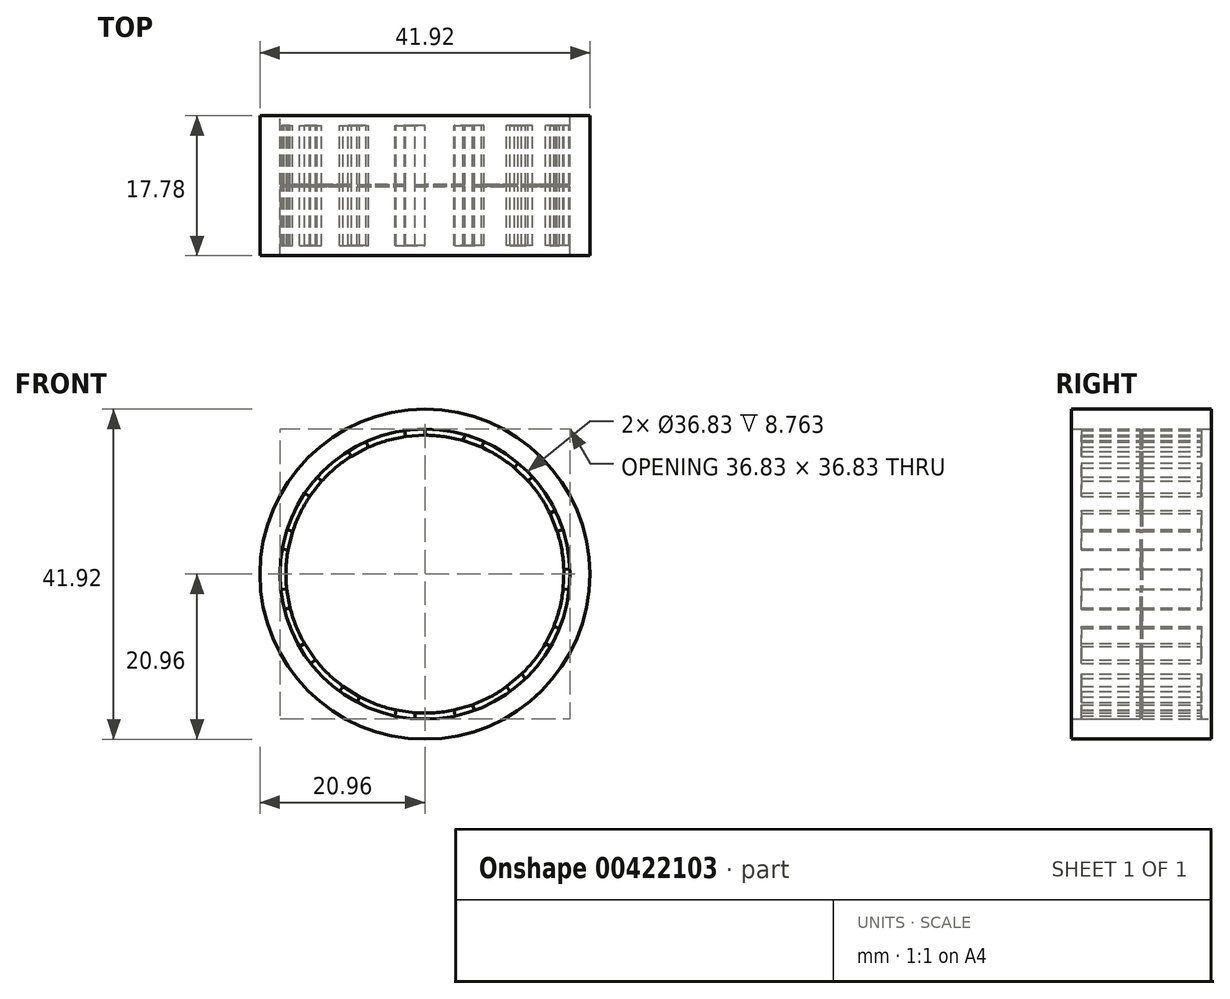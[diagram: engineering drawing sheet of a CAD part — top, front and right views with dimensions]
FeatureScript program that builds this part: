
annotation { "Feature Type Name" : "Feature", "Feature Type Description" : "" }
export const myFeature = defineFeature(function(context is Context, id is Id, definition is map)
    precondition{}
    {
        {
            var Q0;
            Q0=qCreatedBy(makeId("Front.planeOp"),FACE);
            var sketch = newSketch(context, id + "F0", { "sketchPlane" : qUnion([Q0])});
            skCircle(sketch, "E0", {"center": v(0, 0) * mm, "radius": 20.96 * mm});
            skCircle(sketch, "E1", {"center": v(0, 0) * mm, "radius": 18.41 * mm});
            skSolve(sketch);
        }
        {
            var Q0;
            Q0=makeQuery(id+"F0.imprint","IMPRINT",FACE,{"disambiguationData":[TD([[makeQuery(id+"F0.imprint","IMPRINT",EDGE,{"derivedFrom":sQuery(id+"F0.wireOp",EDGE,"E1")}),1.0]])]});
            var sketch = newSketch(context, id + "F1", { "sketchPlane" : qUnion([Q0])});
            skLineSegment(sketch, "E2", {"start": v(0, 18.41) * mm, "end": v(0, 17.65) * mm});
            skLineSegment(sketch, "E3", {"start": v(-2.56, 18.24) * mm, "end": v(-2.46, 17.48) * mm});
            skLineSegment(sketch, "E4", {"start": v(-2.46, 17.48) * mm, "end": v(0, 17.65) * mm});
            skArc(sketch, "E5", {"start": v(0, 18.41) * mm, "mid": v(-1.3, 18.5) * mm, "end": v(-2.56, 18.24) * mm});
            skLineSegment(sketch, "E6.1.0", {"start": v(-7.5, 16.82) * mm, "end": v(-7.18, 16.13) * mm});
            skArc(sketch, "E6.1.1", {"start": v(-7.5, 16.82) * mm, "mid": v(-8.7, 16.37) * mm, "end": v(-9.76, 15.62) * mm});
            skLineSegment(sketch, "E6.1.2", {"start": v(-9.35, 14.97) * mm, "end": v(-7.18, 16.13) * mm});
            skLineSegment(sketch, "E6.1.3", {"start": v(-9.76, 15.62) * mm, "end": v(-9.35, 14.97) * mm});
            skLineSegment(sketch, "E6.2.0", {"start": v(-13.69, 12.32) * mm, "end": v(-13.12, 11.81) * mm});
            skArc(sketch, "E6.2.1", {"start": v(-13.69, 12.32) * mm, "mid": v(-14.6, 11.41) * mm, "end": v(-15.27, 10.3) * mm});
            skLineSegment(sketch, "E6.2.2", {"start": v(-14.64, 9.87) * mm, "end": v(-13.12, 11.81) * mm});
            skLineSegment(sketch, "E6.2.3", {"start": v(-15.27, 10.3) * mm, "end": v(-14.64, 9.87) * mm});
            skLineSegment(sketch, "E6.3.0", {"start": v(-17.51, 5.7) * mm, "end": v(-16.79, 5.46) * mm});
            skArc(sketch, "E6.3.1", {"start": v(-17.51, 5.7) * mm, "mid": v(-17.99, 4.49) * mm, "end": v(-18.14, 3.2) * mm});
            skLineSegment(sketch, "E6.3.2", {"start": v(-17.38, 3.07) * mm, "end": v(-16.79, 5.46) * mm});
            skLineSegment(sketch, "E6.3.3", {"start": v(-18.14, 3.2) * mm, "end": v(-17.38, 3.07) * mm});
            skLineSegment(sketch, "E6.4.0", {"start": v(-18.31, -1.92) * mm, "end": v(-17.56, -1.85) * mm});
            skArc(sketch, "E6.4.1", {"start": v(-18.31, -1.92) * mm, "mid": v(-18.26, -3.22) * mm, "end": v(-17.87, -4.45) * mm});
            skLineSegment(sketch, "E6.4.2", {"start": v(-17.13, -4.27) * mm, "end": v(-17.56, -1.85) * mm});
            skLineSegment(sketch, "E6.4.3", {"start": v(-17.87, -4.45) * mm, "end": v(-17.13, -4.27) * mm});
            skLineSegment(sketch, "E6.5.0", {"start": v(-15.95, -9.2) * mm, "end": v(-15.29, -8.83) * mm});
            skArc(sketch, "E6.5.1", {"start": v(-15.95, -9.2) * mm, "mid": v(-15.37, -10.37) * mm, "end": v(-14.51, -11.34) * mm});
            skLineSegment(sketch, "E6.5.2", {"start": v(-13.91, -10.87) * mm, "end": v(-15.29, -8.83) * mm});
            skLineSegment(sketch, "E6.5.3", {"start": v(-14.51, -11.34) * mm, "end": v(-13.91, -10.87) * mm});
            skLineSegment(sketch, "E6.6.0", {"start": v(-10.82, -14.9) * mm, "end": v(-10.38, -14.28) * mm});
            skArc(sketch, "E6.6.1", {"start": v(-10.82, -14.9) * mm, "mid": v(-9.82, -15.72) * mm, "end": v(-8.65, -16.26) * mm});
            skLineSegment(sketch, "E6.6.2", {"start": v(-8.29, -15.59) * mm, "end": v(-10.38, -14.28) * mm});
            skLineSegment(sketch, "E6.6.3", {"start": v(-8.65, -16.26) * mm, "end": v(-8.29, -15.59) * mm});
            skLineSegment(sketch, "E6.7.0", {"start": v(-3.83, -18.01) * mm, "end": v(-3.67, -17.27) * mm});
            skArc(sketch, "E6.7.1", {"start": v(-3.83, -18.01) * mm, "mid": v(-2.58, -18.36) * mm, "end": v(-1.28, -18.37) * mm});
            skLineSegment(sketch, "E6.7.2", {"start": v(-1.23, -17.6) * mm, "end": v(-3.67, -17.27) * mm});
            skLineSegment(sketch, "E6.7.3", {"start": v(-1.28, -18.37) * mm, "end": v(-1.23, -17.6) * mm});
            skLineSegment(sketch, "E6.8.0", {"start": v(3.83, -18.01) * mm, "end": v(3.67, -17.27) * mm});
            skArc(sketch, "E6.8.1", {"start": v(3.83, -18.01) * mm, "mid": v(5.11, -17.82) * mm, "end": v(6.3, -17.3) * mm});
            skLineSegment(sketch, "E6.8.2", {"start": v(6.04, -16.59) * mm, "end": v(3.67, -17.27) * mm});
            skLineSegment(sketch, "E6.8.3", {"start": v(6.3, -17.3) * mm, "end": v(6.04, -16.59) * mm});
            skLineSegment(sketch, "E6.9.0", {"start": v(10.82, -14.9) * mm, "end": v(10.38, -14.28) * mm});
            skArc(sketch, "E6.9.1", {"start": v(10.82, -14.9) * mm, "mid": v(11.92, -14.2) * mm, "end": v(12.8, -13.25) * mm});
            skLineSegment(sketch, "E6.9.2", {"start": v(12.26, -12.7) * mm, "end": v(10.38, -14.28) * mm});
            skLineSegment(sketch, "E6.9.3", {"start": v(12.8, -13.25) * mm, "end": v(12.26, -12.7) * mm});
            skLineSegment(sketch, "E6.10.0", {"start": v(15.95, -9.2) * mm, "end": v(15.29, -8.83) * mm});
            skArc(sketch, "E6.10.1", {"start": v(15.95, -9.2) * mm, "mid": v(16.66, -8.13) * mm, "end": v(17.07, -6.9) * mm});
            skLineSegment(sketch, "E6.10.2", {"start": v(16.37, -6.61) * mm, "end": v(15.29, -8.83) * mm});
            skLineSegment(sketch, "E6.10.3", {"start": v(17.07, -6.9) * mm, "end": v(16.37, -6.61) * mm});
            skLineSegment(sketch, "E6.11.0", {"start": v(18.31, -1.92) * mm, "end": v(17.56, -1.85) * mm});
            skArc(sketch, "E6.11.1", {"start": v(18.31, -1.92) * mm, "mid": v(18.53, -0.65) * mm, "end": v(18.4, 0.64) * mm});
            skLineSegment(sketch, "E6.11.2", {"start": v(17.64, 0.62) * mm, "end": v(17.56, -1.85) * mm});
            skLineSegment(sketch, "E6.11.3", {"start": v(18.4, 0.64) * mm, "end": v(17.64, 0.62) * mm});
            skLineSegment(sketch, "E6.12.0", {"start": v(17.51, 5.7) * mm, "end": v(16.79, 5.46) * mm});
            skArc(sketch, "E6.12.1", {"start": v(17.51, 5.7) * mm, "mid": v(17.2, 6.95) * mm, "end": v(16.55, 8.07) * mm});
            skLineSegment(sketch, "E6.12.2", {"start": v(15.87, 7.74) * mm, "end": v(16.79, 5.46) * mm});
            skLineSegment(sketch, "E6.12.3", {"start": v(16.55, 8.07) * mm, "end": v(15.87, 7.74) * mm});
            skLineSegment(sketch, "E6.13.0", {"start": v(13.69, 12.32) * mm, "end": v(13.12, 11.81) * mm});
            skArc(sketch, "E6.13.1", {"start": v(13.69, 12.32) * mm, "mid": v(12.88, 13.34) * mm, "end": v(11.84, 14.1) * mm});
            skLineSegment(sketch, "E6.13.2", {"start": v(11.35, 13.52) * mm, "end": v(13.12, 11.81) * mm});
            skLineSegment(sketch, "E6.13.3", {"start": v(11.84, 14.1) * mm, "end": v(11.35, 13.52) * mm});
            skLineSegment(sketch, "E6.14.0", {"start": v(7.5, 16.82) * mm, "end": v(7.18, 16.13) * mm});
            skArc(sketch, "E6.14.1", {"start": v(7.5, 16.82) * mm, "mid": v(6.34, 17.42) * mm, "end": v(5.08, 17.7) * mm});
            skLineSegment(sketch, "E6.14.2", {"start": v(4.87, 16.97) * mm, "end": v(7.18, 16.13) * mm});
            skLineSegment(sketch, "E6.14.3", {"start": v(5.08, 17.7) * mm, "end": v(4.87, 16.97) * mm});
            skPoint(sketch, "E6.center", {"position": v(0, 0) * mm});
            skSolve(sketch);
        }
        {
            var Q0;
            {var subQ1=sQuery(id+"F1.wireOp",EDGE,"E2");Q0=makeQuery(id+"F1.imprint","IMPRINT",FACE,{"disambiguationData":[TD([[makeQuery(id+"F1.imprint","IMPRINT",EDGE,{"derivedFrom":subQ1}),1.0]])]});}
            var sketch = newSketch(context, id + "F2", { "sketchPlane" : qUnion([Q0])});
            skCircle(sketch, "E7", {"center": v(0, 0) * mm, "radius": 17.65 * mm});
            skSolve(sketch);
        }
        {
            var Q0;
            Q0 = qSketchRegion(id + "F0", true);
            extrude(context, id + "F3", {"entities" : qUnion([Q0]), "endBound" : BoundingType.SYMMETRIC, "depth" : 17.78 * mm});
        }
        {
            var Q0;
            Q0 = qSketchRegion(id + "F1", true);
            extrude(context, id + "F4", {"entities" : qUnion([Q0]), "operationType" : NewBodyOperationType.ADD, "endBound" : BoundingType.SYMMETRIC, "depth" : 15.24 * mm});
        }
        {
            var Q0;
            {var subQ1=makeQuery(id+"F1.imprint","IMPRINT",EDGE,{"derivedFrom":sQuery(id+"F1.wireOp",EDGE,"E6.12.2")});Q0=makeQuery(id+"F2.imprint","IMPRINT",FACE,{"disambiguationData":[TD([[makeQuery(id+"F2.imprint","IMPRINT",EDGE,{"derivedFrom":subQ1}),1.0]])]});}
            var Q1;
            {var subQ1=makeQuery(id+"F1.imprint","IMPRINT",EDGE,{"derivedFrom":sQuery(id+"F1.wireOp",EDGE,"E6.13.2")});Q1=makeQuery(id+"F2.imprint","IMPRINT",FACE,{"disambiguationData":[TD([[makeQuery(id+"F2.imprint","IMPRINT",EDGE,{"derivedFrom":subQ1}),1.0]])]});}
            var Q2;
            {var subQ1=makeQuery(id+"F1.imprint","IMPRINT",EDGE,{"derivedFrom":sQuery(id+"F1.wireOp",EDGE,"E6.14.2")});Q2=makeQuery(id+"F2.imprint","IMPRINT",FACE,{"disambiguationData":[TD([[makeQuery(id+"F2.imprint","IMPRINT",EDGE,{"derivedFrom":subQ1}),1.0]])]});}
            var Q3;
            {var subQ1=makeQuery(id+"F1.imprint","IMPRINT",EDGE,{"derivedFrom":sQuery(id+"F1.wireOp",EDGE,"E4")});Q3=makeQuery(id+"F2.imprint","IMPRINT",FACE,{"disambiguationData":[TD([[makeQuery(id+"F2.imprint","IMPRINT",EDGE,{"derivedFrom":subQ1}),1.0]])]});}
            var Q4;
            {var subQ1=makeQuery(id+"F1.imprint","IMPRINT",EDGE,{"derivedFrom":sQuery(id+"F1.wireOp",EDGE,"E6.1.2")});Q4=makeQuery(id+"F2.imprint","IMPRINT",FACE,{"disambiguationData":[TD([[makeQuery(id+"F2.imprint","IMPRINT",EDGE,{"derivedFrom":subQ1}),1.0]])]});}
            var Q5;
            {var subQ1=makeQuery(id+"F1.imprint","IMPRINT",EDGE,{"derivedFrom":sQuery(id+"F1.wireOp",EDGE,"E6.2.2")});Q5=makeQuery(id+"F2.imprint","IMPRINT",FACE,{"disambiguationData":[TD([[makeQuery(id+"F2.imprint","IMPRINT",EDGE,{"derivedFrom":subQ1}),1.0]])]});}
            var Q6;
            {var subQ1=makeQuery(id+"F1.imprint","IMPRINT",EDGE,{"derivedFrom":sQuery(id+"F1.wireOp",EDGE,"E6.3.2")});Q6=makeQuery(id+"F2.imprint","IMPRINT",FACE,{"disambiguationData":[TD([[makeQuery(id+"F2.imprint","IMPRINT",EDGE,{"derivedFrom":subQ1}),1.0]])]});}
            var Q7;
            {var subQ1=makeQuery(id+"F1.imprint","IMPRINT",EDGE,{"derivedFrom":sQuery(id+"F1.wireOp",EDGE,"E6.4.2")});Q7=makeQuery(id+"F2.imprint","IMPRINT",FACE,{"disambiguationData":[TD([[makeQuery(id+"F2.imprint","IMPRINT",EDGE,{"derivedFrom":subQ1}),1.0]])]});}
            var Q8;
            {var subQ1=makeQuery(id+"F1.imprint","IMPRINT",EDGE,{"derivedFrom":sQuery(id+"F1.wireOp",EDGE,"E6.5.2")});Q8=makeQuery(id+"F2.imprint","IMPRINT",FACE,{"disambiguationData":[TD([[makeQuery(id+"F2.imprint","IMPRINT",EDGE,{"derivedFrom":subQ1}),1.0]])]});}
            var Q9;
            {var subQ1=makeQuery(id+"F1.imprint","IMPRINT",EDGE,{"derivedFrom":sQuery(id+"F1.wireOp",EDGE,"E6.6.2")});Q9=makeQuery(id+"F2.imprint","IMPRINT",FACE,{"disambiguationData":[TD([[makeQuery(id+"F2.imprint","IMPRINT",EDGE,{"derivedFrom":subQ1}),1.0]])]});}
            var Q10;
            {var subQ1=makeQuery(id+"F1.imprint","IMPRINT",EDGE,{"derivedFrom":sQuery(id+"F1.wireOp",EDGE,"E6.7.2")});Q10=makeQuery(id+"F2.imprint","IMPRINT",FACE,{"disambiguationData":[TD([[makeQuery(id+"F2.imprint","IMPRINT",EDGE,{"derivedFrom":subQ1}),1.0]])]});}
            var Q11;
            {var subQ1=makeQuery(id+"F1.imprint","IMPRINT",EDGE,{"derivedFrom":sQuery(id+"F1.wireOp",EDGE,"E6.8.2")});Q11=makeQuery(id+"F2.imprint","IMPRINT",FACE,{"disambiguationData":[TD([[makeQuery(id+"F2.imprint","IMPRINT",EDGE,{"derivedFrom":subQ1}),1.0]])]});}
            var Q12;
            {var subQ1=makeQuery(id+"F1.imprint","IMPRINT",EDGE,{"derivedFrom":sQuery(id+"F1.wireOp",EDGE,"E6.9.2")});Q12=makeQuery(id+"F2.imprint","IMPRINT",FACE,{"disambiguationData":[TD([[makeQuery(id+"F2.imprint","IMPRINT",EDGE,{"derivedFrom":subQ1}),1.0]])]});}
            var Q13;
            {var subQ1=makeQuery(id+"F1.imprint","IMPRINT",EDGE,{"derivedFrom":sQuery(id+"F1.wireOp",EDGE,"E6.10.2")});Q13=makeQuery(id+"F2.imprint","IMPRINT",FACE,{"disambiguationData":[TD([[makeQuery(id+"F2.imprint","IMPRINT",EDGE,{"derivedFrom":subQ1}),1.0]])]});}
            var Q14;
            {var subQ1=makeQuery(id+"F1.imprint","IMPRINT",EDGE,{"derivedFrom":sQuery(id+"F1.wireOp",EDGE,"E6.11.2")});Q14=makeQuery(id+"F2.imprint","IMPRINT",FACE,{"disambiguationData":[TD([[makeQuery(id+"F2.imprint","IMPRINT",EDGE,{"derivedFrom":subQ1}),1.0]])]});}
            var Q15;
            {var subQ1=sQuery(id+"F1.wireOp",EDGE,"E6.2.3");var subQ2=makeQuery(id+"F1.imprint","IMPRINT",EDGE,{"derivedFrom":subQ1});Q15=makeQuery(id+"F2.imprint","IMPRINT",FACE,{"disambiguationData":[TD([[makeQuery(id+"F2.imprint","IMPRINT",EDGE,{"derivedFrom":subQ2}),-1.0]])]});}
            var Q16;
            {var subQ1=sQuery(id+"F1.wireOp",EDGE,"E6.1.3");var subQ2=makeQuery(id+"F1.imprint","IMPRINT",EDGE,{"derivedFrom":subQ1});Q16=makeQuery(id+"F2.imprint","IMPRINT",FACE,{"disambiguationData":[TD([[makeQuery(id+"F2.imprint","IMPRINT",EDGE,{"derivedFrom":subQ2}),-1.0]])]});}
            var Q17;
            {var subQ1=sQuery(id+"F1.wireOp",EDGE,"E3");var subQ2=makeQuery(id+"F1.imprint","IMPRINT",EDGE,{"derivedFrom":subQ1});Q17=makeQuery(id+"F2.imprint","IMPRINT",FACE,{"disambiguationData":[TD([[makeQuery(id+"F2.imprint","IMPRINT",EDGE,{"derivedFrom":subQ2}),-1.0]])]});}
            var Q18;
            {var subQ1=sQuery(id+"F1.wireOp",EDGE,"E2");var subQ2=makeQuery(id+"F1.imprint","IMPRINT",EDGE,{"derivedFrom":subQ1});Q18=makeQuery(id+"F2.imprint","IMPRINT",FACE,{"disambiguationData":[TD([[makeQuery(id+"F2.imprint","IMPRINT",EDGE,{"derivedFrom":subQ2}),1.0]])]});}
            var Q19;
            {var subQ1=sQuery(id+"F1.wireOp",EDGE,"E6.13.3");var subQ2=makeQuery(id+"F1.imprint","IMPRINT",EDGE,{"derivedFrom":subQ1});Q19=makeQuery(id+"F2.imprint","IMPRINT",FACE,{"disambiguationData":[TD([[makeQuery(id+"F2.imprint","IMPRINT",EDGE,{"derivedFrom":subQ2}),-1.0]])]});}
            var Q20;
            {var subQ1=sQuery(id+"F1.wireOp",EDGE,"E6.12.3");var subQ2=makeQuery(id+"F1.imprint","IMPRINT",EDGE,{"derivedFrom":subQ1});Q20=makeQuery(id+"F2.imprint","IMPRINT",FACE,{"disambiguationData":[TD([[makeQuery(id+"F2.imprint","IMPRINT",EDGE,{"derivedFrom":subQ2}),-1.0]])]});}
            var Q21;
            {var subQ1=sQuery(id+"F1.wireOp",EDGE,"E6.3.3");var subQ2=makeQuery(id+"F1.imprint","IMPRINT",EDGE,{"derivedFrom":subQ1});Q21=makeQuery(id+"F2.imprint","IMPRINT",FACE,{"disambiguationData":[TD([[makeQuery(id+"F2.imprint","IMPRINT",EDGE,{"derivedFrom":subQ2}),-1.0]])]});}
            var Q22;
            {var subQ1=sQuery(id+"F1.wireOp",EDGE,"E6.4.3");var subQ2=makeQuery(id+"F1.imprint","IMPRINT",EDGE,{"derivedFrom":subQ1});Q22=makeQuery(id+"F2.imprint","IMPRINT",FACE,{"disambiguationData":[TD([[makeQuery(id+"F2.imprint","IMPRINT",EDGE,{"derivedFrom":subQ2}),-1.0]])]});}
            var Q23;
            {var subQ1=sQuery(id+"F1.wireOp",EDGE,"E6.5.3");var subQ2=makeQuery(id+"F1.imprint","IMPRINT",EDGE,{"derivedFrom":subQ1});Q23=makeQuery(id+"F2.imprint","IMPRINT",FACE,{"disambiguationData":[TD([[makeQuery(id+"F2.imprint","IMPRINT",EDGE,{"derivedFrom":subQ2}),-1.0]])]});}
            var Q24;
            {var subQ1=sQuery(id+"F1.wireOp",EDGE,"E6.7.3");var subQ2=makeQuery(id+"F1.imprint","IMPRINT",EDGE,{"derivedFrom":subQ1});Q24=makeQuery(id+"F2.imprint","IMPRINT",FACE,{"disambiguationData":[TD([[makeQuery(id+"F2.imprint","IMPRINT",EDGE,{"derivedFrom":subQ2}),-1.0]])]});}
            var Q25;
            {var subQ1=sQuery(id+"F1.wireOp",EDGE,"E6.6.3");var subQ2=makeQuery(id+"F1.imprint","IMPRINT",EDGE,{"derivedFrom":subQ1});Q25=makeQuery(id+"F2.imprint","IMPRINT",FACE,{"disambiguationData":[TD([[makeQuery(id+"F2.imprint","IMPRINT",EDGE,{"derivedFrom":subQ2}),-1.0]])]});}
            var Q26;
            {var subQ1=sQuery(id+"F1.wireOp",EDGE,"E6.10.3");var subQ2=makeQuery(id+"F1.imprint","IMPRINT",EDGE,{"derivedFrom":subQ1});Q26=makeQuery(id+"F2.imprint","IMPRINT",FACE,{"disambiguationData":[TD([[makeQuery(id+"F2.imprint","IMPRINT",EDGE,{"derivedFrom":subQ2}),-1.0]])]});}
            var Q27;
            {var subQ1=sQuery(id+"F1.wireOp",EDGE,"E6.11.3");var subQ2=makeQuery(id+"F1.imprint","IMPRINT",EDGE,{"derivedFrom":subQ1});Q27=makeQuery(id+"F2.imprint","IMPRINT",FACE,{"disambiguationData":[TD([[makeQuery(id+"F2.imprint","IMPRINT",EDGE,{"derivedFrom":subQ2}),-1.0]])]});}
            var Q28;
            {var subQ1=sQuery(id+"F1.wireOp",EDGE,"E6.9.3");var subQ2=makeQuery(id+"F1.imprint","IMPRINT",EDGE,{"derivedFrom":subQ1});Q28=makeQuery(id+"F2.imprint","IMPRINT",FACE,{"disambiguationData":[TD([[makeQuery(id+"F2.imprint","IMPRINT",EDGE,{"derivedFrom":subQ2}),-1.0]])]});}
            var Q29;
            {var subQ1=sQuery(id+"F1.wireOp",EDGE,"E6.8.3");var subQ2=makeQuery(id+"F1.imprint","IMPRINT",EDGE,{"derivedFrom":subQ1});Q29=makeQuery(id+"F2.imprint","IMPRINT",FACE,{"disambiguationData":[TD([[makeQuery(id+"F2.imprint","IMPRINT",EDGE,{"derivedFrom":subQ2}),-1.0]])]});}
            extrude(context, id + "F5", {"entities" : qUnion([Q0, Q1, Q2, Q3, Q4, Q5, Q6, Q7, Q8, Q9, Q10, Q11, Q12, Q13, Q14, Q15, Q16, Q17, Q18, Q19, Q20, Q21, Q22, Q23, Q24, Q25, Q26, Q27, Q28, Q29]), "operationType" : NewBodyOperationType.ADD, "endBound" : BoundingType.SYMMETRIC, "depth" : 0.25 * mm});
        }
    });
